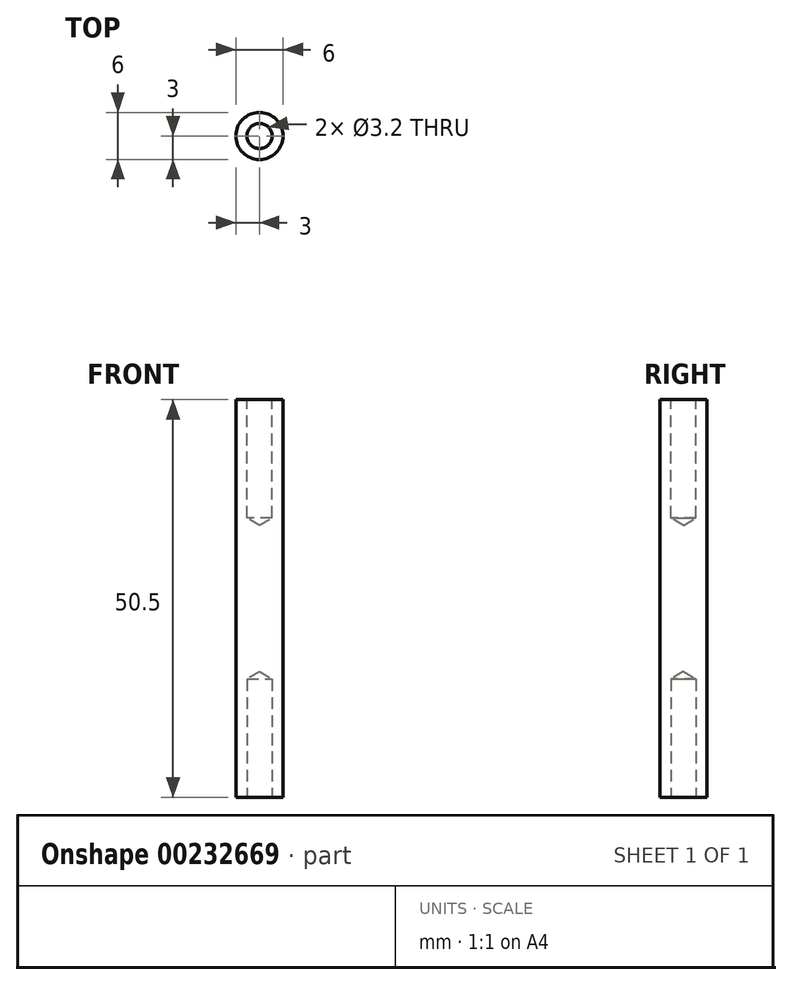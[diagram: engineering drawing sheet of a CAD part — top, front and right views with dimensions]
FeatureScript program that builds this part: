
annotation { "Feature Type Name" : "Feature", "Feature Type Description" : "" }
export const myFeature = defineFeature(function(context is Context, id is Id, definition is map)
    precondition{}
    {
        {
            var Q0;
            Q0=qCreatedBy(makeId("Top.planeOp"),FACE);
            var sketch = newSketch(context, id + "F0", { "sketchPlane" : qUnion([Q0])});
            skCircle(sketch, "E0", {"center": v(0, 0) * mm, "radius": 3 * mm});
            skSolve(sketch);
        }
        {
            var Q0;
            Q0=makeQuery(id+"F0.imprint","IMPRINT",FACE,{"disambiguationData":[TD([[makeQuery(id+"F0.imprint","IMPRINT",EDGE,{"derivedFrom":sQuery(id+"F0.wireOp",EDGE,"E0")}),1.0]])]});
            extrude(context, id + "F1", {"entities" : qUnion([Q0]), "depth" : 50.5 * mm});
        }
        {
            var Q0;
            Q0=sQuery(id+"F0.wireOp",VERTEX,"E0.center");
            var Q1;
            Q1=makeQuery(id+"F1.opExtrude","SWEPT_BODY",BODY,{"disambiguationData":[OSD([sQuery(id+"F0.wireOp",EDGE,"E0")])]});
            hole(context, id + "F2", {"style" : HoleStyle.SIMPLE, "endStyle" : HoleEndStyle.BLIND, "oppositeDirection" : true, "standardTappedOrClearance" : lookupTablePath({ "standard" : "ISO", "engagement" : "75%", "pitch" : "0.75 mm", "size" : "M4", "type" : "Tapped" }), "standardBlindInLast" : lookupTablePath({ "standard" : "ISO", "engagement" : "75%", "pitch" : "0.75 mm", "size" : "M4", "type" : "Tapped" }), "holeDiameter" : 3.2 * mm, "holeDepth" : 15 * mm, "locations" : qUnion([Q0]), "scope" : qUnion([Q1])});
        }
        {
            var Q0;
            Q0=makeQuery(id+"F1.opExtrude","CAP_FACE",FACE,{"disambiguationData":[OSD([sQuery(id+"F0.wireOp",EDGE,"E0")])],"isStart":false});
            var sketch = newSketch(context, id + "F3", { "sketchPlane" : qUnion([Q0])});
            skPoint(sketch, "E1", {"position": v(0, 0) * mm});
            skSolve(sketch);
        }
        {
            var Q0;
            Q0=sQuery(id+"F3.wireOp",VERTEX,"E1");
            var Q1;
            Q1=makeQuery(id+"F1.opExtrude","SWEPT_BODY",BODY,{"disambiguationData":[OSD([sQuery(id+"F0.wireOp",EDGE,"E0")])]});
            hole(context, id + "F4", {"style" : HoleStyle.SIMPLE, "endStyle" : HoleEndStyle.BLIND, "standardTappedOrClearance" : lookupTablePath({ "standard" : "ISO", "engagement" : "75%", "pitch" : "0.75 mm", "size" : "M4", "type" : "Tapped" }), "standardBlindInLast" : lookupTablePath({ "standard" : "ISO", "engagement" : "75%", "pitch" : "0.75 mm", "size" : "M4", "type" : "Tapped" }), "holeDiameter" : 3.2 * mm, "holeDepth" : 15 * mm, "locations" : qUnion([Q0]), "scope" : qUnion([Q1])});
        }
    });
